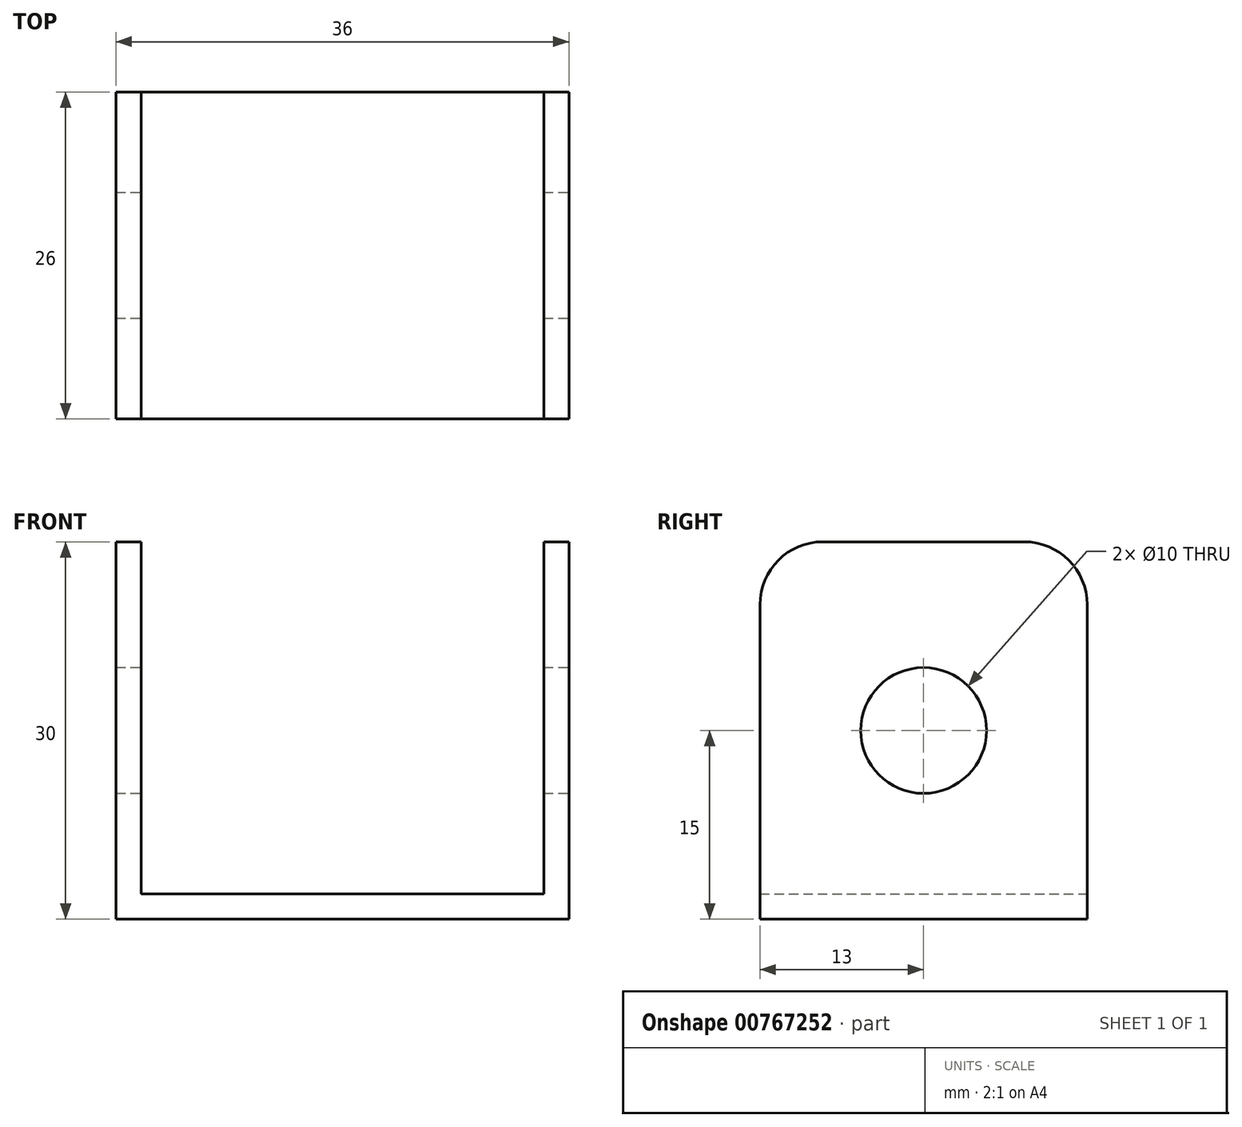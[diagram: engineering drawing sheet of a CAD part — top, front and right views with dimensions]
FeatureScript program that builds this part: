
annotation { "Feature Type Name" : "Feature", "Feature Type Description" : "" }
export const myFeature = defineFeature(function(context is Context, id is Id, definition is map)
    precondition{}
    {
        {
            var Q0;
            Q0=qCreatedBy(makeId("Front.planeOp"),FACE);
            var sketch = newSketch(context, id + "F0", { "sketchPlane" : qUnion([Q0])});
            skLineSegment(sketch, "E0", {"start": v(0, 0) * mm, "end": v(-18, 0) * mm});
            skLineSegment(sketch, "E1", {"start": v(0, 0) * mm, "end": v(18, 0) * mm});
            skLineSegment(sketch, "E2", {"start": v(-18, 0) * mm, "end": v(-18, 30) * mm});
            skLineSegment(sketch, "E3", {"start": v(18, 0) * mm, "end": v(18, 30) * mm});
            skLineSegment(sketch, "E4", {"start": v(-18, 30) * mm, "end": v(-16, 30) * mm});
            skLineSegment(sketch, "E5", {"start": v(-16, 30) * mm, "end": v(-16, 2) * mm});
            skLineSegment(sketch, "E6", {"start": v(-16, 2) * mm, "end": v(16, 2) * mm});
            skLineSegment(sketch, "E7", {"start": v(18, 30) * mm, "end": v(16, 30) * mm});
            skLineSegment(sketch, "E8", {"start": v(16, 30) * mm, "end": v(16, 2) * mm});
            skSolve(sketch);
        }
        {
            var Q0;
            Q0 = qSketchRegion(id + "F0", true);
            extrude(context, id + "F1", {"entities" : qUnion([Q0]), "depth" : 26 * mm, "offsetDistance" : 25 * mm});
        }
        {
            var Q0;
            Q0=makeQuery(id+"F1.opExtrude","SWEPT_FACE",FACE,{"disambiguationData":[OSD([sQuery(id+"F0.wireOp",EDGE,"E3")])]});
            var sketch = newSketch(context, id + "F2", { "sketchPlane" : qUnion([Q0])});
            skCircle(sketch, "E9", {"center": v(-13, 15) * mm, "radius": 5 * mm});
            skPoint(sketch, "E10.orphan", {"position": v(0, 15) * mm});
            skPoint(sketch, "E11.start.orphan", {"position": v(-26, 15) * mm});
            skSolve(sketch);
        }
        {
            var Q0;
            Q0 = qSketchRegion(id + "F2", true);
            extrude(context, id + "F3", {"entities" : qUnion([Q0]), "operationType" : NewBodyOperationType.REMOVE, "oppositeDirection" : true, "depth" : 40 * mm, "offsetDistance" : 25 * mm});
        }
        {
            var Q0;
            Q0=makeQuery(id+"F1.opExtrude","CAP_EDGE",EDGE,{"disambiguationData":[OSD([sQuery(id+"F0.wireOp",EDGE,"E7")])],"isStart":false});
            var Q1;
            Q1=makeQuery(id+"F1.opExtrude","CAP_EDGE",EDGE,{"disambiguationData":[OSD([sQuery(id+"F0.wireOp",EDGE,"E7")])],"isStart":true});
            var Q2;
            Q2=makeQuery(id+"F1.opExtrude","CAP_EDGE",EDGE,{"disambiguationData":[OSD([sQuery(id+"F0.wireOp",EDGE,"E4")])],"isStart":true});
            var Q3;
            Q3=makeQuery(id+"F1.opExtrude","CAP_EDGE",EDGE,{"disambiguationData":[OSD([sQuery(id+"F0.wireOp",EDGE,"E4")])],"isStart":false});
            fillet(context, id + "F4", {"entities" : qUnion([Q0, Q1, Q2, Q3]), "radius" : 5 * mm, "tangentPropagation" : true, "allowEdgeOverflow" : false});
        }
    });
